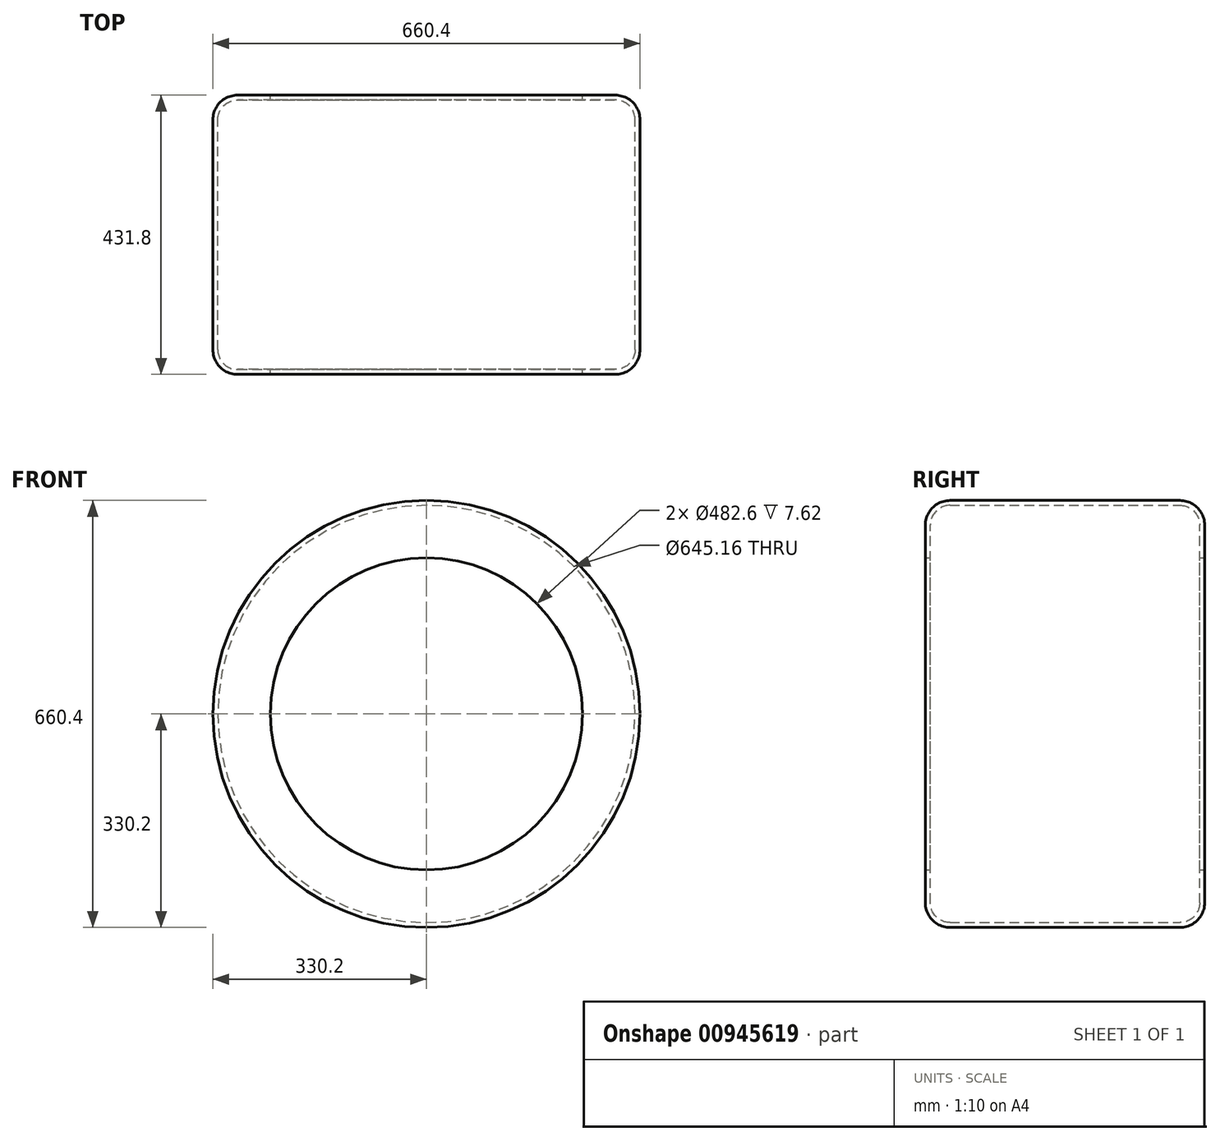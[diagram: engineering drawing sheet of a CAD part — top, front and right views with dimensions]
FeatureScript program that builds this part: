
annotation { "Feature Type Name" : "Feature", "Feature Type Description" : "" }
export const myFeature = defineFeature(function(context is Context, id is Id, definition is map)
    precondition{}
    {
        {
            var Q0;
            Q0=qCreatedBy(makeId("Front.planeOp"),FACE);
            var sketch = newSketch(context, id + "F0", { "sketchPlane" : qUnion([Q0])});
            skCircle(sketch, "E0", {"center": v(0, 0) * mm, "radius": 241.3 * mm});
            skCircle(sketch, "E1", {"center": v(0, 0) * mm, "radius": 330.2 * mm});
            skSolve(sketch);
        }
        {
            var Q0;
            Q0 = qSketchRegion(id + "F0", true);
            extrude(context, id + "F1", {"entities" : qUnion([Q0]), "depth" : 431.8 * mm, "offsetDistance" : 25.4 * mm});
        }
        {
            var Q0;
            Q0=makeQuery(id+"F1.opExtrude","CAP_EDGE",EDGE,{"disambiguationData":[OSD([sQuery(id+"F0.wireOp",EDGE,"E1")])],"isStart":false});
            var Q1;
            Q1=makeQuery(id+"F1.opExtrude","CAP_EDGE",EDGE,{"disambiguationData":[OSD([sQuery(id+"F0.wireOp",EDGE,"E1")])],"isStart":true});
            fillet(context, id + "F2", {"entities" : qUnion([Q0, Q1]), "radius" : 38.1 * mm, "tangentPropagation" : true, "allowEdgeOverflow" : false});
        }
        {
            var Q0;
            Q0=makeQuery(id+"F1.opExtrude","SWEPT_FACE",FACE,{"disambiguationData":[OSD([sQuery(id+"F0.wireOp",EDGE,"E0")])]});
            shell(context, id + "F3", {"entities" : qUnion([Q0]), "thickness" : 7.62 * mm});
        }
        {
            var Q0;
            Q0=qCreatedBy(makeId("Top.planeOp"),FACE);
            cPlane(context, id + "F4", {"entities" : qUnion([Q0]), "cplaneType" : CPlaneType.OFFSET, "offset" : 317.5 * mm, "width" : 152.4 * mm, "height" : 152.4 * mm});
        }
    });
